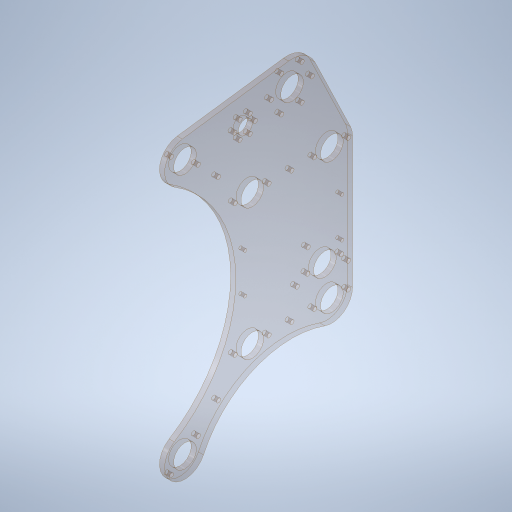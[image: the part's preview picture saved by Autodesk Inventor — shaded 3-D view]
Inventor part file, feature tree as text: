
AUTODESK INVENTOR PART (.ipt)
format: ipt  version: 2023.4 (Build 274418000, 418)  size: 472,576 bytes
history: native  units: in
note: dims shown in document units (in); Inventor stores cm internally (conversion verified against a paired STEP export)
features: sketch x6, hole x5, projected_geometry x2, extrude x1
ambient origin geometry x8: Origin, YZ Plane, XZ Plane, XY Plane, X Axis, Y Axis, Z Axis, Center Point
bodies: Solid1 (feature_tree)
feature tree (14):
  sketch  "Sketch1"  dims[d0=1.0in d1=2.0in]
  sketch  "Sketch2"  dims[d2=3.0in d4=3.8976in]
  extrude  "Extrusion1"  Depth=1.0in
  hole  "Hole1"  [1 undecoded]
  hole  "Hole2"  [1 undecoded]
  hole  "Hole3"  [1 undecoded]
  hole  "Hole4"  [1 undecoded]
  hole  "Hole5"  [1 undecoded]
  sketch  "Sketch3"  dims[d5=3.6869in d6=12.0in]
  sketch  "Sketch4"  dims[d7=0.125in d8=0.125in]
  projected_geometry  "Projected Loop1"
  sketch  "Sketch5"  dims[d9=5.0in d10=15.0in]
  sketch  "Sketch6"  dims[d11=2.0in d12=2.0in d13=4.4882in d14=11.0in d15=1.115in d16=1.5in d17=3.095in d18=2.0in d19=0.25in d31=1.655in d32=0.375in d33=0.25in d34=0.0in d35=1.9488in d36=1.5in d37=1.0in d38=0.69in d50=0.5in d51=0.5in d52=0.201in d53=0.75in d54=0.385in d55=0.25in d56=0.5635in d57=1.0in d58=0.8108in d59=2.3622in d61=360.0deg d63=2.9551in d64=3.0in d68=4.25in d69=1.0in d70=3.0in d71=2.5in d72=3.2185in d73=6.4369in d74=4.7835in d75=1.7in d77=2.0in d78=2.3622in d80=360.0deg d82=0.201in d83=0.75in d84=0.385in d85=0.25in d86=0.5635in d87=1.0in d88=0.8108in d89=0.201in d90=0.328in d91=0.385in d92=0.25in d93=0.5635in d94=1.0in d95=0.8108in d97=1.5in d98=2.517in d99=2.517in d101=0.481in d102=1.25in d104=0.201in d105=0.75in d106=0.375in d107=0.25in d108=0.5635in d109=1.0in d110=0.8108in d111=0.375in d112=0.375in d113=0.375in d114=1.9366in d115=0.5in d116=1.9366in d117=4.75in d118=0.15in d119=0.75in d120=0.279in d121=0.25in d122=0.5635in d123=1.0in d124=0.8108in]
  projected_geometry  "Project Cut Edges1"
note: 5 required parameter values undecoded (feature->parameter linkage not recoverable at this tier; creation-order binding heuristic only, values carry confidence <= 0.55)
